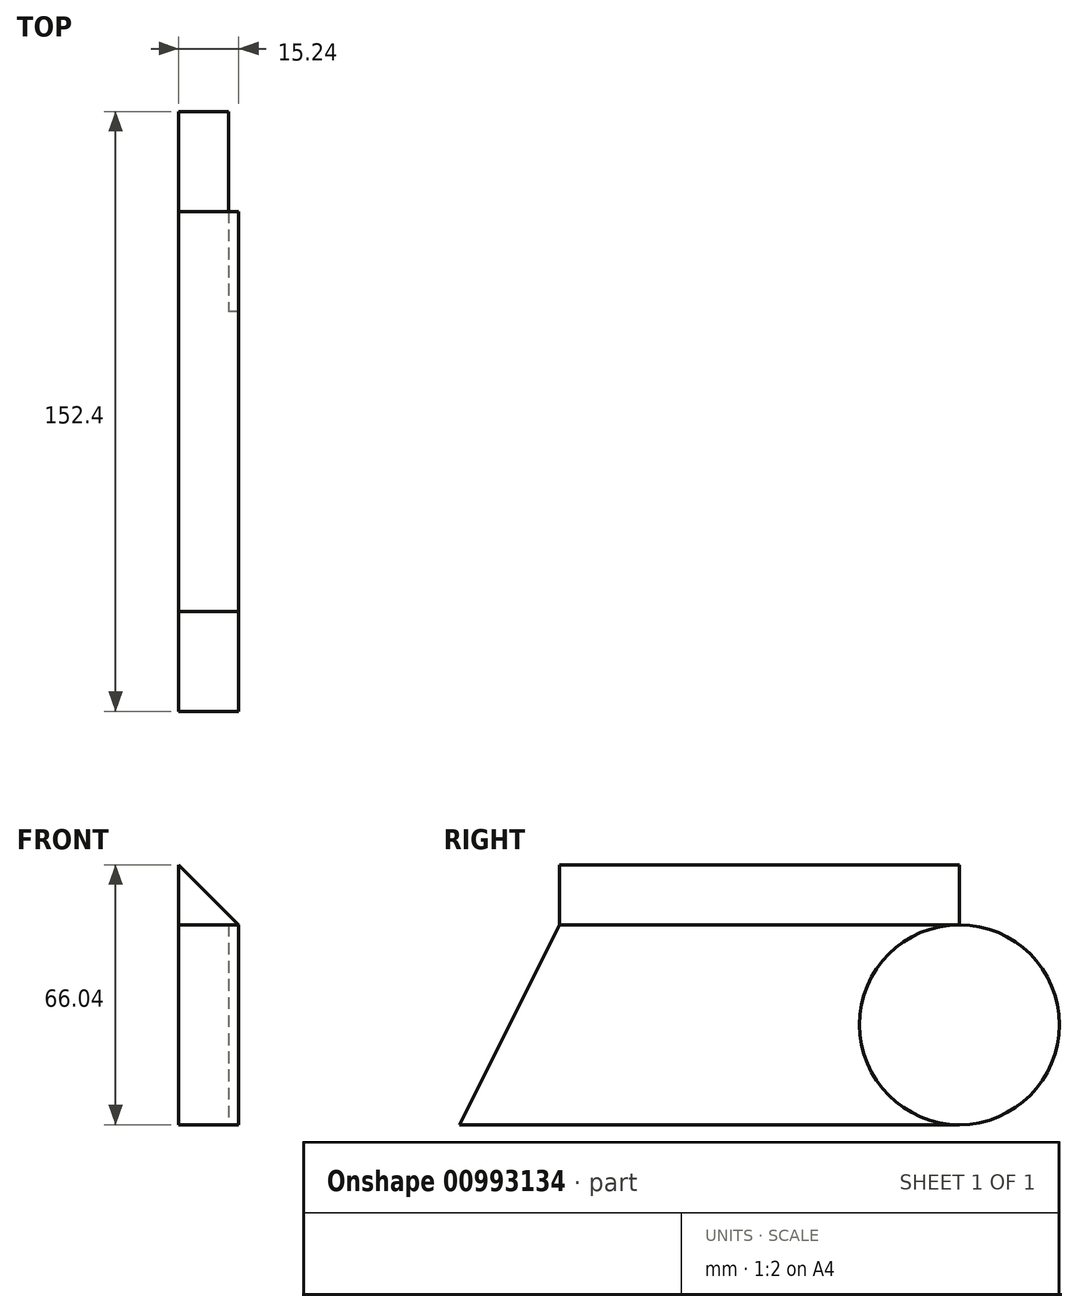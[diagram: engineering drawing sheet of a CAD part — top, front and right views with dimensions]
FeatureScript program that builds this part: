
annotation { "Feature Type Name" : "Feature", "Feature Type Description" : "" }
export const myFeature = defineFeature(function(context is Context, id is Id, definition is map)
    precondition{}
    {
        {
            var Q0;
            Q0=qCreatedBy(makeId("Right.planeOp"),FACE);
            var sketch = newSketch(context, id + "F0", { "sketchPlane" : qUnion([Q0])});
            skLineSegment(sketch, "E0", {"start": v(62.58, 20.67) * mm, "end": v(-77.12, 20.67) * mm});
            skCircle(sketch, "E1", {"center": v(37.18, 20.67) * mm, "radius": 25.4 * mm});
            skLineSegment(sketch, "E2", {"start": v(-77.12, 20.67) * mm, "end": v(-89.82, -4.73) * mm});
            skLineSegment(sketch, "E3", {"start": v(-89.82, -4.73) * mm, "end": v(37.18, -4.73) * mm});
            skPoint(sketch, "E4.startSnap0", {"position": v(-26.32, -4.73) * mm});
            skLineSegment(sketch, "E5", {"start": v(-77.12, 20.67) * mm, "end": v(-64.42, 46.07) * mm});
            skLineSegment(sketch, "E6", {"start": v(-64.42, 46.07) * mm, "end": v(37.18, 46.07) * mm});
            skSolve(sketch);
        }
        {
            var Q0;
            {var subQ4=sQuery(id+"F0.wireOp",EDGE,"E4");Q0=makeQuery(id+"F0.imprint","IMPRINT",FACE,{"disambiguationData":[TD([[makeQuery(id+"F0.imprint","IMPRINT",EDGE,{"derivedFrom":subQ4}),-1.0]])]});}
            var Q1;
            {var subQ0=sQuery(id+"F0.wireOp",EDGE,"E2");Q1=makeQuery(id+"F0.imprint","IMPRINT",FACE,{"disambiguationData":[TD([[makeQuery(id+"F0.imprint","IMPRINT",EDGE,{"derivedFrom":subQ0}),1.0]])]});}
            var Q2;
            {var subQ0=sQuery(id+"F0.wireOp",EDGE,"E5");Q2=makeQuery(id+"F0.imprint","IMPRINT",FACE,{"disambiguationData":[TD([[makeQuery(id+"F0.imprint","IMPRINT",EDGE,{"derivedFrom":subQ0}),-1.0]])]});}
            extrude(context, id + "F1", {"entities" : qUnion([Q0, Q1, Q2]), "depth" : 15.24 * mm, "offsetDistance" : 25.4 * mm});
        }
        {
            var Q0;
            {var subQ0=sQuery(id+"F0.wireOp",EDGE,"E1");var subQ1=sQuery(id+"F0.wireOp",EDGE,"E0");var subQ2=makeQuery(id+"F0.imprint","INTERSECT",VERTEX,{"disambiguationData":[OD(0.0)],"derivedFrom":[subQ1,subQ0]});Q0=makeQuery(id+"F0.imprint","IMPRINT",FACE,{"disambiguationData":[TD([[makeQuery(id+"F0.imprint","IMPRINT",EDGE,{"disambiguationData":[TD([[subQ2,-1.0]])],"derivedFrom":subQ1}),-1.0]])]});}
            var Q1;
            {var subQ0=sQuery(id+"F0.wireOp",EDGE,"E1");var subQ1=sQuery(id+"F0.wireOp",EDGE,"E0");var subQ2=makeQuery(id+"F0.imprint","INTERSECT",VERTEX,{"disambiguationData":[OD(0.0)],"derivedFrom":[subQ1,subQ0]});Q1=makeQuery(id+"F0.imprint","IMPRINT",FACE,{"disambiguationData":[TD([[makeQuery(id+"F0.imprint","IMPRINT",EDGE,{"disambiguationData":[TD([[subQ2,-1.0]])],"derivedFrom":subQ1}),1.0]])]});}
            extrude(context, id + "F2", {"entities" : qUnion([Q0, Q1]), "operationType" : NewBodyOperationType.ADD, "depth" : 12.7 * mm, "offsetDistance" : 25.4 * mm});
        }
        {
            var Q0;
            Q0=makeQuery(id+"F1.opExtrude","SWEPT_FACE",FACE,{"disambiguationData":[OSD([sQuery(id+"F0.wireOp",EDGE,"E6")])]});
            extrude(context, id + "F3", {"entities" : qUnion([Q0]), "operationType" : NewBodyOperationType.ADD, "depth" : 15.24 * mm, "offsetDistance" : 25.4 * mm});
        }
        {
            var Q0;
            Q0=makeQuery(id+"F3.opExtrude","SWEPT_FACE",FACE,{"disambiguationData":[OSD([sQuery(id+"F0.wireOp",EDGE,"E5"),sQuery(id+"F0.wireOp",EDGE,"E6")])]});
            var sketch = newSketch(context, id + "F4", { "sketchPlane" : qUnion([Q0])});
            skLineSegment(sketch, "E7", {"start": v(0, 61.3) * mm, "end": v(15.24, 46.07) * mm});
            skSolve(sketch);
        }
        {
            var Q0;
            Q0=makeQuery(id+"F4.imprint","IMPRINT",FACE,{"disambiguationData":[TD([[makeQuery(id+"F4.imprint","IMPRINT",EDGE,{"derivedFrom":sQuery(id+"F4.wireOp",EDGE,"E7")}),1.0]])]});
            extrude(context, id + "F5", {"entities" : qUnion([Q0]), "operationType" : NewBodyOperationType.REMOVE, "oppositeDirection" : true, "depth" : 101.6 * mm, "offsetDistance" : 25.4 * mm});
        }
    });
